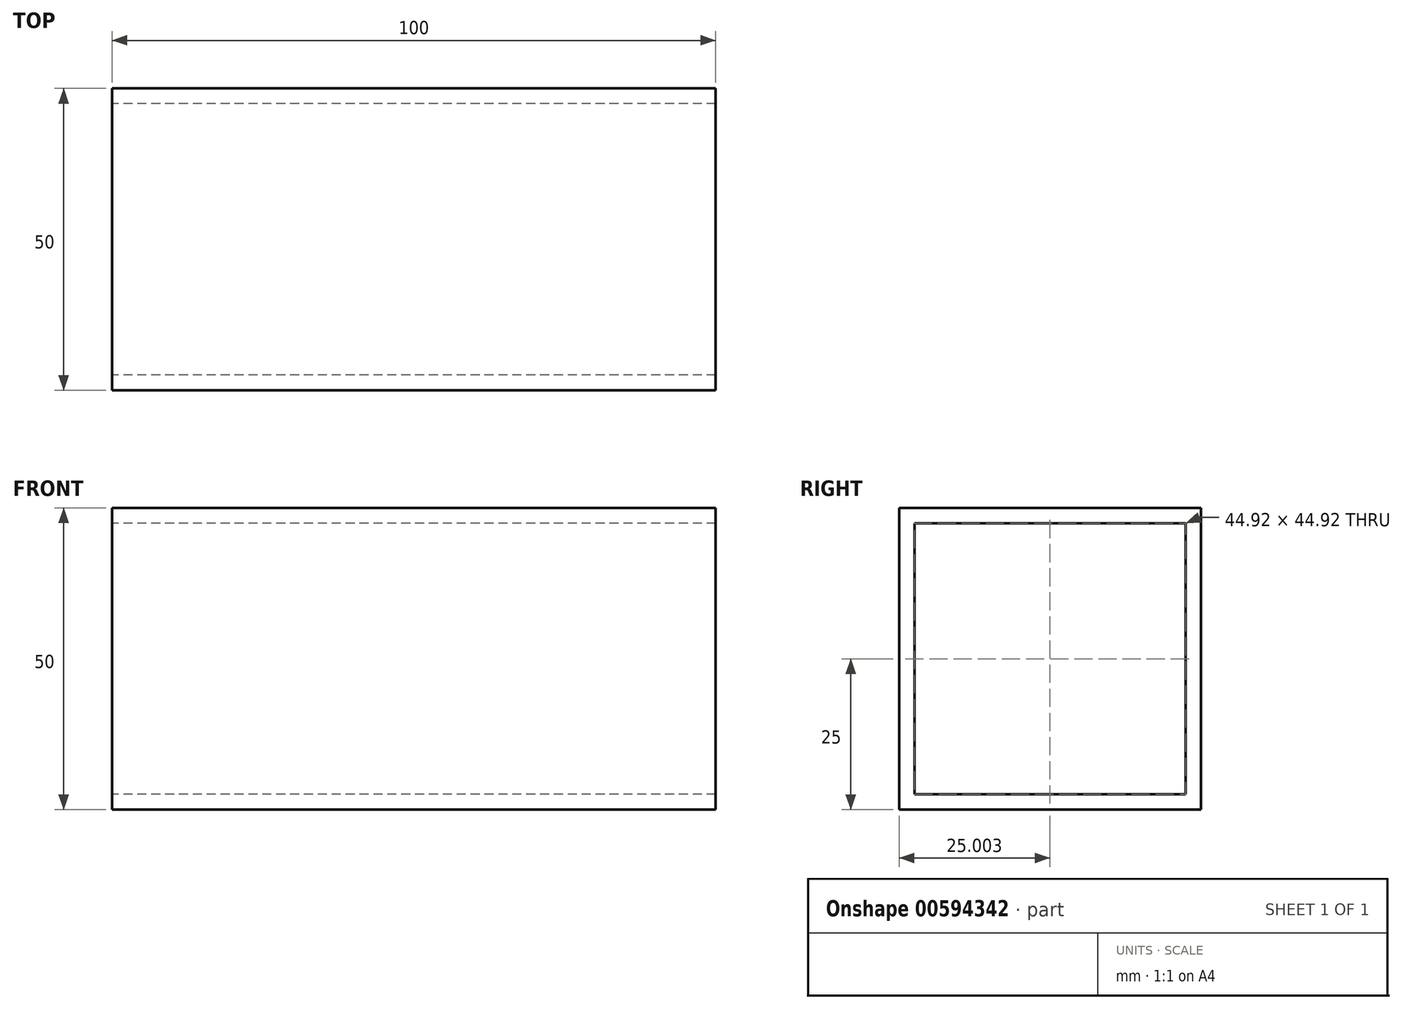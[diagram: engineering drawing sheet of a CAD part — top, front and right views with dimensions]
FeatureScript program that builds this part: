
annotation { "Feature Type Name" : "Feature", "Feature Type Description" : "" }
export const myFeature = defineFeature(function(context is Context, id is Id, definition is map)
    precondition{}
    {
        {
            var Q0;
            Q0=qCreatedBy(makeId("Top.planeOp"),FACE);
            var sketch = newSketch(context, id + "F0", { "sketchPlane" : qUnion([Q0])});
            skLineSegment(sketch, "E0.bottom", {"start": v(58.75, -22.77) * mm, "end": v(-41.25, -22.77) * mm});
            skLineSegment(sketch, "E0.top", {"start": v(58.75, 27.23) * mm, "end": v(-41.25, 27.23) * mm});
            skLineSegment(sketch, "E0.left", {"start": v(58.75, -22.77) * mm, "end": v(58.75, 27.23) * mm});
            skLineSegment(sketch, "E0.right", {"start": v(-41.25, -22.77) * mm, "end": v(-41.25, 27.23) * mm});
            skPoint(sketch, "E0.middle", {"position": v(8.75, 2.23) * mm});
            skSolve(sketch);
        }
        {
            var Q0;
            Q0=makeQuery(id+"F0.imprint","IMPRINT",FACE,{"disambiguationData":[TD([[makeQuery(id+"F0.imprint","IMPRINT",EDGE,{"derivedFrom":sQuery(id+"F0.wireOp",EDGE,"E0.bottom")}),-1.0]])]});
            extrude(context, id + "F1", {"entities" : qUnion([Q0]), "depth" : 50 * mm, "offsetDistance" : 25.4 * mm});
        }
        {
            var Q0;
            Q0=makeQuery(id+"F1.opExtrude","SWEPT_FACE",FACE,{"disambiguationData":[OSD([sQuery(id+"F0.wireOp",EDGE,"E0.left")])]});
            var Q1;
            Q1=makeQuery(id+"F1.opExtrude","SWEPT_FACE",FACE,{"disambiguationData":[OSD([sQuery(id+"F0.wireOp",EDGE,"E0.right")])]});
            shell(context, id + "F2", {"entities" : qUnion([Q0, Q1]), "thickness" : 2.54 * mm});
        }
    });
